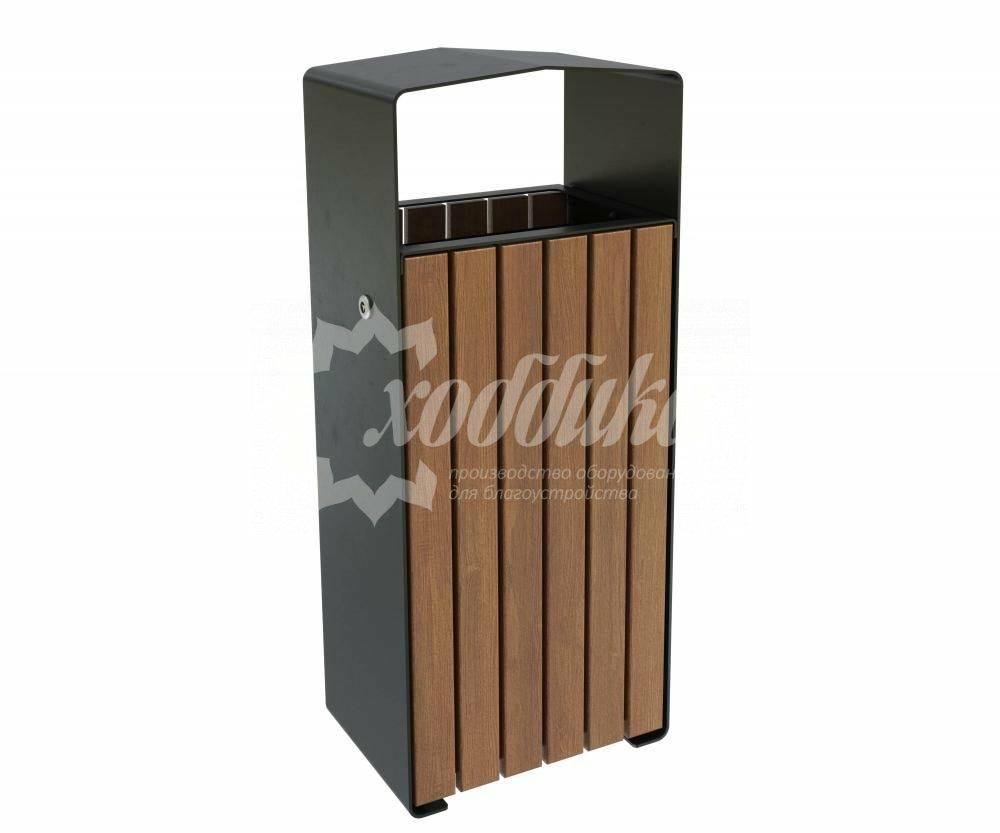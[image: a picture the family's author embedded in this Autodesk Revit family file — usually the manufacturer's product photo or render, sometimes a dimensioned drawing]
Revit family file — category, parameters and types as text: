
# Revit family: Урна стальная «Новая Москва» Арт 12144
name_source: partatom
category: Антураж
revit_build: Autodesk Revit 2018 (Build: 20180423_1000(x64)
units: mm (PartAtom-declared; Revit-internal decimal feet)

## family parameters
Всегда вертикально = Да
Источник визуального образа = Геометрия семейства
На основе рабочей плоскости = Нет
Общий = Нет
При загрузке вырезать с полостями = Нет
Точка расчета площади = Нет

## types (2) — shared parameters
URL = https://hobbyka.ru
Артикул товара = Арт. 12144
Высота = 830 мм
Группа модели = Уличные урны
Длина = 350 мм
Изготовитель = ООО «Хоббика»
Изображение типоразмера = Урна стальная «Новая Москва» Арт 12144.jpg
Цвет отделки = Дерево
Ширина = 250 мм

## per-type parameters (varying)
| type | Материал изделия | Нержавеющая сталь | Объем 25 литрой | Цвет урны |
| Урна стальная «Новая Москва». Версия объем 25 литров | Сталь, дерево | Нет | Да | Сталь |
| Урна стальная «Новая Москва». Версия Нержавеющая сталь | Нержавеющая сталь, дерево | Да | Нет | Нержавеющая сталь |

note: column(s) folded — value = type name in every type: Описание
